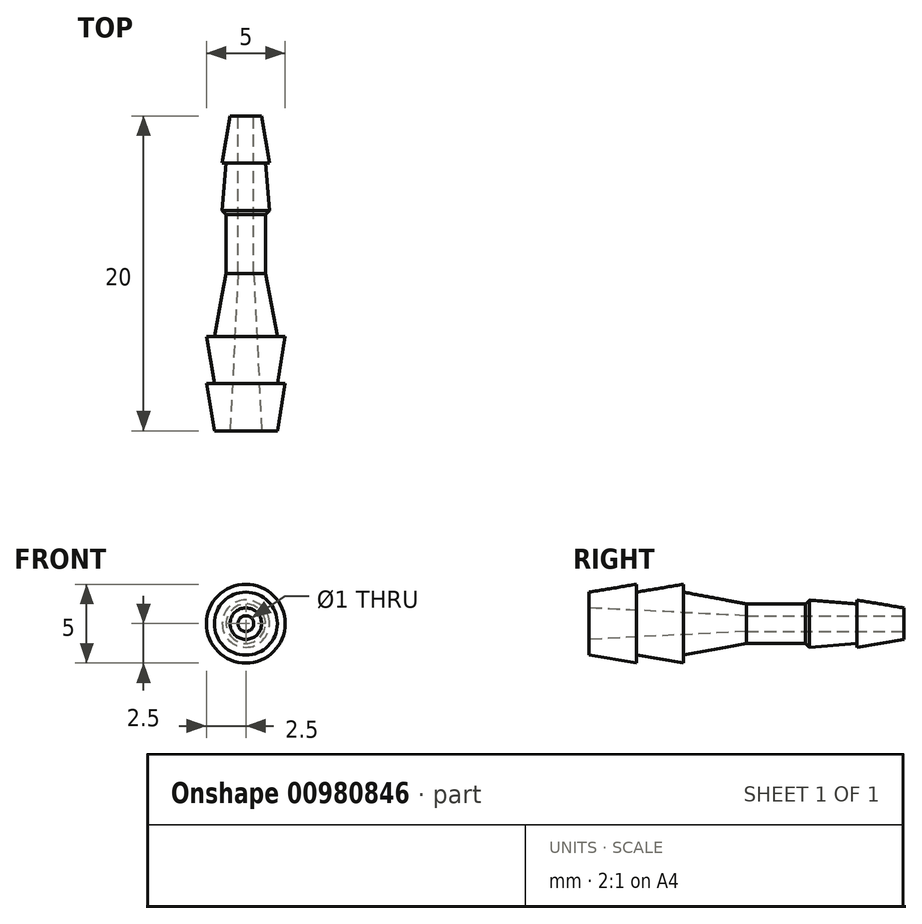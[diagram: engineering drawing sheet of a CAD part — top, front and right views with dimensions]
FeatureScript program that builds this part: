
annotation { "Feature Type Name" : "Feature", "Feature Type Description" : "" }
export const myFeature = defineFeature(function(context is Context, id is Id, definition is map)
    precondition{}
    {
        {
            var Q0;
            Q0=qCreatedBy(makeId("Top.planeOp"),FACE);
            var sketch = newSketch(context, id + "F0", { "sketchPlane" : qUnion([Q0])});
            skLineSegment(sketch, "E0", {"start": v(0.5, 10) * mm, "end": v(1, 10) * mm});
            skLineSegment(sketch, "E1", {"start": v(1, 10) * mm, "end": v(1.5, 7) * mm});
            skLineSegment(sketch, "E2", {"start": v(1.5, 7) * mm, "end": v(1.25, 7) * mm});
            skLineSegment(sketch, "E3", {"start": v(1.25, 7) * mm, "end": v(1.5, 4) * mm});
            skLineSegment(sketch, "E4", {"start": v(1.5, 4) * mm, "end": v(1.25, 3.75) * mm});
            skLineSegment(sketch, "E5", {"start": v(1.25, 3.75) * mm, "end": v(1.25, 0) * mm});
            skLineSegment(sketch, "E6", {"start": v(1.25, 0) * mm, "end": v(1.5, -1.34) * mm});
            skLineSegment(sketch, "E7", {"start": v(1.5, -1.34) * mm, "end": v(2, -4) * mm});
            skLineSegment(sketch, "E8", {"start": v(2, -4) * mm, "end": v(2.5, -4) * mm});
            skLineSegment(sketch, "E9", {"start": v(2.5, -4) * mm, "end": v(2, -7) * mm});
            skLineSegment(sketch, "E10", {"start": v(2, -7) * mm, "end": v(2.5, -7) * mm});
            skLineSegment(sketch, "E11", {"start": v(2.5, -7) * mm, "end": v(2, -10) * mm});
            skLineSegment(sketch, "E12", {"start": v(2, -10) * mm, "end": v(1, -10) * mm});
            skLineSegment(sketch, "E13", {"start": v(0.5, 10) * mm, "end": v(0.5, 0) * mm});
            skLineSegment(sketch, "E14", {"start": v(0.5, 0) * mm, "end": v(1, -10) * mm});
            skLineSegment(sketch, "E15", {"start": v(0, 22.27) * mm, "end": v(0, -13.44) * mm, "construction": true});
            skSolve(sketch);
        }
        {
            var Q0;
            Q0 = qSketchRegion(id + "F0", true);
            var Q1;
            Q1=sQuery(id+"F0.wireOp",EDGE,"E15");
            revolve(context, id + "F1", {"surfaceOperationType" : NewSurfaceOperationType.NEW, "entities" : qUnion([Q0]), "axis" : qUnion([Q1]), "revolveType" : RevolveType.FULL});
        }
    });
